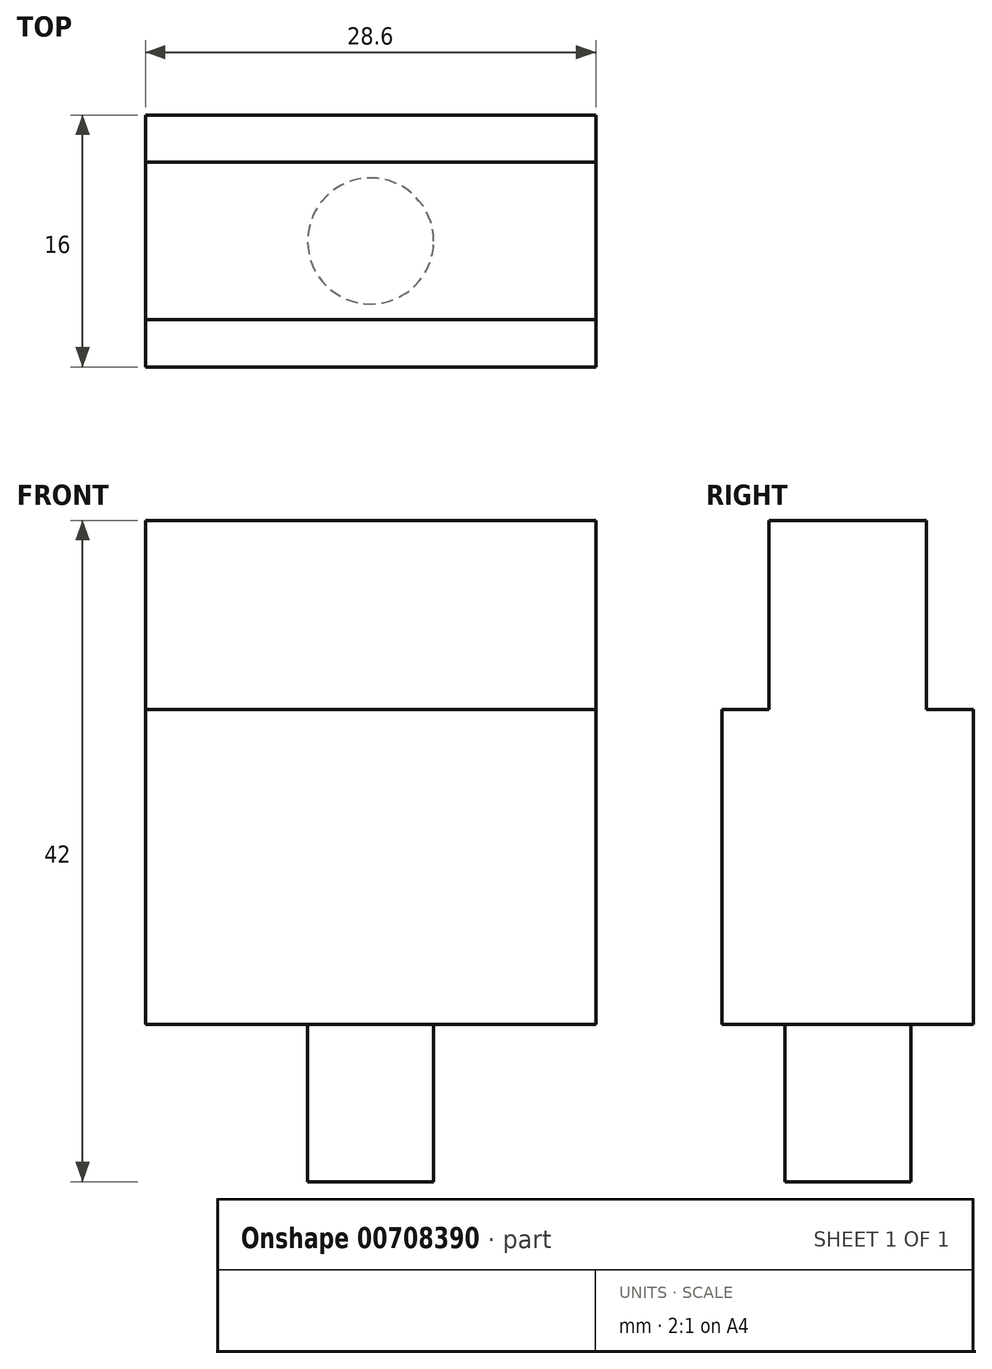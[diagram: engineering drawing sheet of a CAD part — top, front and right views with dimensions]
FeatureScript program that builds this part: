
annotation { "Feature Type Name" : "Feature", "Feature Type Description" : "" }
export const myFeature = defineFeature(function(context is Context, id is Id, definition is map)
    precondition{}
    {
        {
            var Q0;
            Q0=qCreatedBy(makeId("Top.planeOp"),FACE);
            var sketch = newSketch(context, id + "F0", { "sketchPlane" : qUnion([Q0])});
            skLineSegment(sketch, "E0.bottom", {"start": v(0, 0) * mm, "end": v(28.6, 0) * mm});
            skLineSegment(sketch, "E0.top", {"start": v(0, 16) * mm, "end": v(28.6, 16) * mm});
            skLineSegment(sketch, "E0.left", {"start": v(0, 0) * mm, "end": v(0, 16) * mm});
            skLineSegment(sketch, "E0.right", {"start": v(28.6, 0) * mm, "end": v(28.6, 16) * mm});
            skSolve(sketch);
        }
        {
            var Q0;
            Q0=makeQuery(id+"F0.imprint","IMPRINT",FACE,{"disambiguationData":[TD([[makeQuery(id+"F0.imprint","IMPRINT",EDGE,{"derivedFrom":sQuery(id+"F0.wireOp",EDGE,"E0.bottom")}),1.0]])]});
            extrude(context, id + "F1", {"entities" : qUnion([Q0]), "depth" : 20 * mm, "offsetDistance" : 25 * mm});
        }
        {
            var Q0;
            Q0=makeQuery(id+"F1.opExtrude","CAP_FACE",FACE,{"disambiguationData":[OSD([sQuery(id+"F0.wireOp",EDGE,"E0.bottom"),sQuery(id+"F0.wireOp",EDGE,"E0.top"),sQuery(id+"F0.wireOp",EDGE,"E0.left"),sQuery(id+"F0.wireOp",EDGE,"E0.right")])],"isStart":false});
            var sketch = newSketch(context, id + "F2", { "sketchPlane" : qUnion([Q0])});
            skLineSegment(sketch, "E1.bottom", {"start": v(0, 3) * mm, "end": v(28.6, 3) * mm});
            skLineSegment(sketch, "E1.top", {"start": v(0, 13) * mm, "end": v(28.6, 13) * mm});
            skLineSegment(sketch, "E1.left", {"start": v(0, 3) * mm, "end": v(0, 13) * mm});
            skLineSegment(sketch, "E1.right", {"start": v(28.6, 3) * mm, "end": v(28.6, 13) * mm});
            skSolve(sketch);
        }
        {
            var Q0;
            Q0=makeQuery(id+"F2.imprint","IMPRINT",FACE,{"disambiguationData":[TD([[makeQuery(id+"F2.imprint","IMPRINT",EDGE,{"derivedFrom":sQuery(id+"F2.wireOp",EDGE,"E1.bottom")}),1.0]])]});
            extrude(context, id + "F3", {"entities" : qUnion([Q0]), "operationType" : NewBodyOperationType.ADD, "depth" : 12 * mm, "offsetDistance" : 25 * mm});
        }
        {
            var Q0;
            Q0=makeQuery(id+"F1.opExtrude","CAP_FACE",FACE,{"disambiguationData":[OSD([sQuery(id+"F0.wireOp",EDGE,"E0.bottom"),sQuery(id+"F0.wireOp",EDGE,"E0.top"),sQuery(id+"F0.wireOp",EDGE,"E0.left"),sQuery(id+"F0.wireOp",EDGE,"E0.right")])],"isStart":true});
            var sketch = newSketch(context, id + "F4", { "sketchPlane" : qUnion([Q0])});
            skCircle(sketch, "E2", {"center": v(14.3, -8) * mm, "radius": 4 * mm});
            skPoint(sketch, "E2.centerSnap0", {"position": v(14.3, 0) * mm});
            skPoint(sketch, "E2.centerSnap1", {"position": v(0, -8) * mm});
            skSolve(sketch);
        }
        {
            var Q0;
            Q0=makeQuery(id+"F4.imprint","IMPRINT",FACE,{"disambiguationData":[TD([[makeQuery(id+"F4.imprint","IMPRINT",EDGE,{"derivedFrom":sQuery(id+"F4.wireOp",EDGE,"E2")}),1.0]])]});
            extrude(context, id + "F5", {"entities" : qUnion([Q0]), "operationType" : NewBodyOperationType.ADD, "depth" : 10 * mm, "offsetDistance" : 25 * mm});
        }
    });
